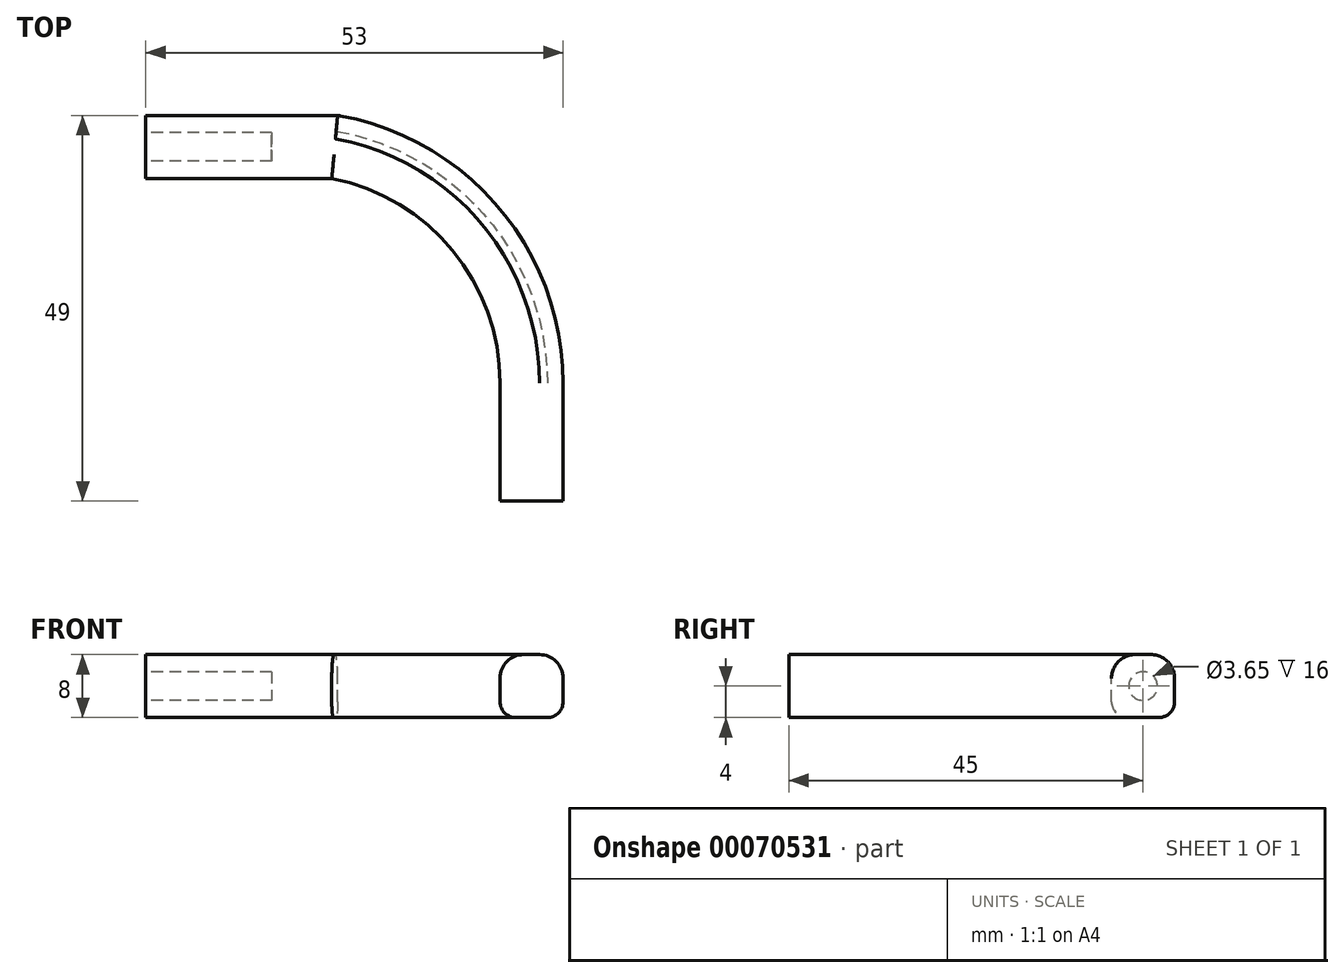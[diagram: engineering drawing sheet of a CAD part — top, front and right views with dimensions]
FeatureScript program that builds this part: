
annotation { "Feature Type Name" : "Feature", "Feature Type Description" : "" }
export const myFeature = defineFeature(function(context is Context, id is Id, definition is map)
    precondition{}
    {
        {
            var Q0;
            Q0=qCreatedBy(makeId("Top.planeOp"),FACE);
            var sketch = newSketch(context, id + "F0", { "sketchPlane" : qUnion([Q0])});
            skLineSegment(sketch, "E0", {"start": v(0, 0) * mm, "end": v(24, 0) * mm});
            skLineSegment(sketch, "E1.bottom", {"start": v(24, 0) * mm, "end": v(49, 0) * mm, "construction": true});
            skLineSegment(sketch, "E1.top", {"start": v(24, -30) * mm, "end": v(49, -30) * mm, "construction": true});
            skLineSegment(sketch, "E1.left", {"start": v(24, 0) * mm, "end": v(24, -30) * mm, "construction": true});
            skLineSegment(sketch, "E1.right", {"start": v(49, 0) * mm, "end": v(49, -30) * mm, "construction": true});
            skArc(sketch, "E2", {"start": v(49, -30) * mm, "mid": v(41.93, -10.47) * mm, "end": v(24, 0) * mm});
            skLineSegment(sketch, "E3", {"start": v(49, -30) * mm, "end": v(49, -45) * mm});
            skSolve(sketch);
        }
        {
            var Q0;
            Q0=qCreatedBy(makeId("Right.planeOp"),FACE);
            var sketch = newSketch(context, id + "F1", { "sketchPlane" : qUnion([Q0])});
            skLineSegment(sketch, "E4.rect.bottom", {"start": v(-4, -4) * mm, "end": v(4, -4) * mm});
            skLineSegment(sketch, "E4.rect.top", {"start": v(-4, 4) * mm, "end": v(4, 4) * mm});
            skLineSegment(sketch, "E4.rect.left", {"start": v(-4, -4) * mm, "end": v(-4, 4) * mm});
            skLineSegment(sketch, "E4.rect.right", {"start": v(4, -4) * mm, "end": v(4, 4) * mm});
            skPoint(sketch, "E4.rect.middle", {"position": v(0, 0) * mm});
            skSolve(sketch);
        }
        {
            var Q0;
            Q0=makeQuery(id+"F1.imprint","IMPRINT",FACE,{"disambiguationData":[TD([[makeQuery(id+"F1.imprint","IMPRINT",EDGE,{"derivedFrom":sQuery(id+"F1.wireOp",EDGE,"E4.rect.bottom")}),1.0]])]});
            var Q1;
            Q1=sQuery(id+"F0.wireOp",EDGE,"E0");
            var Q2;
            Q2=sQuery(id+"F0.wireOp",EDGE,"E2");
            var Q3;
            Q3=sQuery(id+"F0.wireOp",EDGE,"E3");
            sweep(context, id + "F2", {"profiles" : qUnion([Q0]), "path" : qUnion([Q1, Q2, Q3])});
        }
        {
            var Q0;
            Q0=makeQuery(id+"F2.opSweep","CAP_FACE",FACE,{"disambiguationData":[OSD([sQuery(id+"F0.wireOp",VERTEX,"E0.start"),sQuery(id+"F1.wireOp",EDGE,"345b8b9d-d963-4c6d-81a3-9d80807bd11b")])],"isStart":true});
            var sketch = newSketch(context, id + "F3", { "sketchPlane" : qUnion([Q0])});
            skCircle(sketch, "E5", {"center": v(0, 0) * mm, "radius": 1.83 * mm});
            skSolve(sketch);
        }
        {
            var Q0;
            Q0=makeQuery(id+"F3.imprint","IMPRINT",FACE,{"disambiguationData":[TD([[makeQuery(id+"F3.imprint","IMPRINT",EDGE,{"derivedFrom":sQuery(id+"F3.wireOp",EDGE,"E5")}),1.0]])]});
            extrude(context, id + "F4", {"entities" : qUnion([Q0]), "operationType" : NewBodyOperationType.REMOVE, "oppositeDirection" : true, "depth" : 16 * mm});
        }
        {
            var Q0;
            Q0=makeQuery(id+"F2.opSweep","SWEPT_EDGE",EDGE,{"disambiguationData":[OSD([sQuery(id+"F0.wireOp",EDGE,"E0"),sQuery(id+"F1.wireOp",EDGE,"E4.rect.top"),sQuery(id+"F1.wireOp",EDGE,"E4.rect.right")])]});
            var Q1;
            Q1=makeQuery(id+"F2.opSweep","SWEPT_EDGE",EDGE,{"disambiguationData":[OSD([sQuery(id+"F0.wireOp",EDGE,"E2"),sQuery(id+"F1.wireOp",EDGE,"E4.rect.top"),sQuery(id+"F1.wireOp",EDGE,"E4.rect.right")]),OD(1.0)]});
            var Q2;
            Q2=makeQuery(id+"F2.opSweep","SWEPT_EDGE",EDGE,{"disambiguationData":[OSD([sQuery(id+"F0.wireOp",EDGE,"E2"),sQuery(id+"F1.wireOp",EDGE,"E4.rect.top"),sQuery(id+"F1.wireOp",EDGE,"E4.rect.left")])]});
            var Q3;
            Q3=makeQuery(id+"F2.opSweep","SWEPT_EDGE",EDGE,{"disambiguationData":[OSD([sQuery(id+"F0.wireOp",EDGE,"E0"),sQuery(id+"F1.wireOp",EDGE,"E4.rect.top"),sQuery(id+"F1.wireOp",EDGE,"E4.rect.left")])]});
            fillet(context, id + "F5", {"entities" : qUnion([Q0, Q1, Q2, Q3]), "radius" : 3 * mm, "tangentPropagation" : true, "allowEdgeOverflow" : false});
        }
        {
            var Q0;
            Q0=makeQuery(id+"F2.opSweep","SWEPT_EDGE",EDGE,{"disambiguationData":[OSD([sQuery(id+"F0.wireOp",EDGE,"E0"),sQuery(id+"F1.wireOp",EDGE,"E4.rect.bottom"),sQuery(id+"F1.wireOp",EDGE,"E4.rect.right")])]});
            var Q1;
            Q1=makeQuery(id+"F2.opSweep","SWEPT_EDGE",EDGE,{"disambiguationData":[OSD([sQuery(id+"F0.wireOp",EDGE,"E2"),sQuery(id+"F1.wireOp",EDGE,"E4.rect.bottom"),sQuery(id+"F1.wireOp",EDGE,"E4.rect.right")]),OD(1.0)]});
            var Q2;
            Q2=makeQuery(id+"F2.opSweep","SWEPT_EDGE",EDGE,{"disambiguationData":[OSD([sQuery(id+"F0.wireOp",EDGE,"E2"),sQuery(id+"F1.wireOp",EDGE,"E4.rect.bottom"),sQuery(id+"F1.wireOp",EDGE,"E4.rect.left")])]});
            var Q3;
            Q3=makeQuery(id+"F2.opSweep","SWEPT_EDGE",EDGE,{"disambiguationData":[OSD([sQuery(id+"F0.wireOp",EDGE,"E0"),sQuery(id+"F1.wireOp",EDGE,"E4.rect.bottom"),sQuery(id+"F1.wireOp",EDGE,"E4.rect.left")])]});
            fillet(context, id + "F6", {"entities" : qUnion([Q0, Q1, Q2, Q3]), "radius" : 2 * mm, "tangentPropagation" : true, "allowEdgeOverflow" : false});
        }
    });
